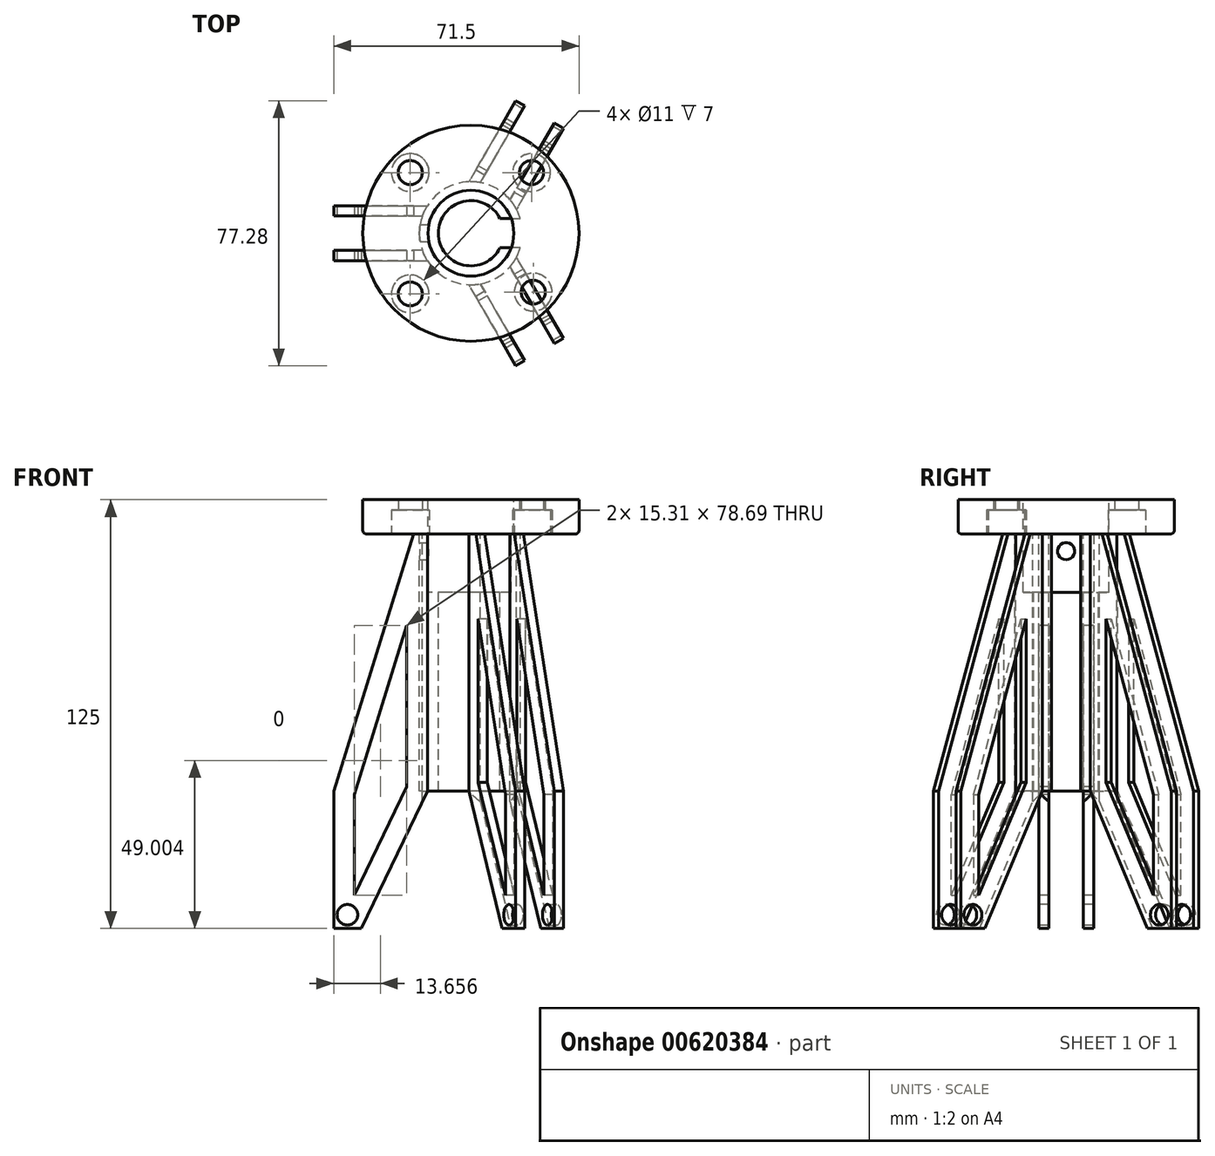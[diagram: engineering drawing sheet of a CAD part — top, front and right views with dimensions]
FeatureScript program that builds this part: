
annotation { "Feature Type Name" : "Feature", "Feature Type Description" : "" }
export const myFeature = defineFeature(function(context is Context, id is Id, definition is map)
    precondition{}
    {
        {
            var Q0;
            Q0=qCreatedBy(makeId("Top.planeOp"),FACE);
            var sketch = newSketch(context, id + "F0", { "sketchPlane" : qUnion([Q0])});
            skCircle(sketch, "E0", {"center": v(0, 0) * mm, "radius": 31.5 * mm});
            skCircle(sketch, "E1", {"center": v(0, 0) * mm, "radius": 25 * mm});
            skLineSegment(sketch, "E2", {"start": v(0, 0) * mm, "end": v(0, 25) * mm});
            skLineSegment(sketch, "E3", {"start": v(0, 0) * mm, "end": v(-17.68, 17.68) * mm});
            skCircle(sketch, "E4", {"center": v(-17.68, 17.68) * mm, "radius": 3.5 * mm});
            skLineSegment(sketch, "E5", {"start": v(0, 0) * mm, "end": v(17.68, 17.68) * mm});
            skLineSegment(sketch, "E6", {"start": v(0, 0) * mm, "end": v(0, -25) * mm});
            skLineSegment(sketch, "E7", {"start": v(0, 0) * mm, "end": v(-17.68, -17.68) * mm});
            skLineSegment(sketch, "E8", {"start": v(0.5, 0.5) * mm, "end": v(18.17, -17.17) * mm});
            skCircle(sketch, "E9", {"center": v(-17.68, -17.68) * mm, "radius": 3.5 * mm});
            skCircle(sketch, "E10", {"center": v(18.17, -17.17) * mm, "radius": 3.5 * mm});
            skCircle(sketch, "E11", {"center": v(17.68, 17.68) * mm, "radius": 3.5 * mm});
            skCircle(sketch, "E12", {"center": v(-17.68, -17.68) * mm, "radius": 5.5 * mm});
            skCircle(sketch, "E13", {"center": v(18.17, -17.17) * mm, "radius": 5.5 * mm});
            skCircle(sketch, "E14", {"center": v(17.68, 17.68) * mm, "radius": 5.5 * mm});
            skCircle(sketch, "E15", {"center": v(-17.68, 17.68) * mm, "radius": 5.5 * mm});
            skSolve(sketch);
        }
        {
            var Q0;
            Q0 = qSketchRegion(id + "F0", true);
            var Q1;
            {var subQ5=sQuery(id+"F0.wireOp",EDGE,"E4");var subQ6=sQuery(id+"F0.wireOp",EDGE,"E1");var subQ7=makeQuery(id+"F0.imprint","INTERSECT",VERTEX,{"disambiguationData":[OD(1.0)],"derivedFrom":[subQ6,subQ5]});Q1=makeQuery(id+"F0.imprint","IMPRINT",FACE,{"disambiguationData":[TD([[makeQuery(id+"F0.imprint","IMPRINT",EDGE,{"disambiguationData":[TD([[subQ7,-1.0]])],"derivedFrom":subQ6}),1.0]])]});}
            var Q2;
            {var subQ0=sQuery(id+"F0.wireOp",EDGE,"E2");Q2=makeQuery(id+"F0.imprint","IMPRINT",FACE,{"disambiguationData":[TD([[makeQuery(id+"F0.imprint","IMPRINT",EDGE,{"derivedFrom":subQ0}),1.0]])]});}
            var Q3;
            {var subQ4=sQuery(id+"F0.wireOp",EDGE,"E2");Q3=makeQuery(id+"F0.imprint","IMPRINT",FACE,{"disambiguationData":[TD([[makeQuery(id+"F0.imprint","IMPRINT",EDGE,{"derivedFrom":subQ4}),-1.0]])]});}
            var Q4;
            {var subQ5=sQuery(id+"F0.wireOp",EDGE,"E6");Q4=makeQuery(id+"F0.imprint","IMPRINT",FACE,{"disambiguationData":[TD([[makeQuery(id+"F0.imprint","IMPRINT",EDGE,{"derivedFrom":subQ5}),1.0]])]});}
            var Q5;
            {var subQ1=sQuery(id+"F0.wireOp",EDGE,"E1");var subQ7=sQuery(id+"F0.wireOp",EDGE,"E11");var subQ9=makeQuery(id+"F0.imprint","INTERSECT",VERTEX,{"disambiguationData":[OD(0.0)],"derivedFrom":[subQ1,subQ7]});Q5=makeQuery(id+"F0.imprint","IMPRINT",FACE,{"disambiguationData":[TD([[makeQuery(id+"F0.imprint","IMPRINT",EDGE,{"disambiguationData":[TD([[subQ9,1.0]])],"derivedFrom":subQ1}),1.0]])]});}
            var Q6;
            {var subQ0=sQuery(id+"F0.wireOp",EDGE,"E6");Q6=makeQuery(id+"F0.imprint","IMPRINT",FACE,{"disambiguationData":[TD([[makeQuery(id+"F0.imprint","IMPRINT",EDGE,{"derivedFrom":subQ0}),-1.0]])]});}
            var Q7;
            {var subQ1=sQuery(id+"F0.wireOp",EDGE,"E1");var subQ7=sQuery(id+"F0.wireOp",EDGE,"E14");var subQ9=makeQuery(id+"F0.imprint","INTERSECT",VERTEX,{"disambiguationData":[OD(0.0)],"derivedFrom":[subQ1,subQ7]});Q7=makeQuery(id+"F0.imprint","IMPRINT",FACE,{"disambiguationData":[TD([[makeQuery(id+"F0.imprint","IMPRINT",EDGE,{"disambiguationData":[TD([[subQ9,1.0]])],"derivedFrom":subQ1}),1.0]])]});}
            var Q8;
            {var subQ1=sQuery(id+"F0.wireOp",EDGE,"E1");var subQ7=sQuery(id+"F0.wireOp",EDGE,"E15");var subQ9=makeQuery(id+"F0.imprint","INTERSECT",VERTEX,{"disambiguationData":[OD(1.0)],"derivedFrom":[subQ1,subQ7]});Q8=makeQuery(id+"F0.imprint","IMPRINT",FACE,{"disambiguationData":[TD([[makeQuery(id+"F0.imprint","IMPRINT",EDGE,{"disambiguationData":[TD([[subQ9,-1.0]])],"derivedFrom":subQ1}),1.0]])]});}
            var Q9;
            {var subQ0=sQuery(id+"F0.wireOp",EDGE,"E10");var subQ1=sQuery(id+"F0.wireOp",EDGE,"E1");var subQ2=makeQuery(id+"F0.imprint","INTERSECT",VERTEX,{"disambiguationData":[OD(1.0)],"derivedFrom":[subQ1,subQ0]});Q9=makeQuery(id+"F0.imprint","IMPRINT",FACE,{"disambiguationData":[TD([[makeQuery(id+"F0.imprint","IMPRINT",EDGE,{"disambiguationData":[TD([[subQ2,-1.0]])],"derivedFrom":subQ1}),1.0]])]});}
            var Q10;
            {var subQ0=sQuery(id+"F0.wireOp",EDGE,"E13");var subQ1=sQuery(id+"F0.wireOp",EDGE,"E1");var subQ2=makeQuery(id+"F0.imprint","INTERSECT",VERTEX,{"disambiguationData":[OD(0.0)],"derivedFrom":[subQ1,subQ0]});Q10=makeQuery(id+"F0.imprint","IMPRINT",FACE,{"disambiguationData":[TD([[makeQuery(id+"F0.imprint","IMPRINT",EDGE,{"disambiguationData":[TD([[subQ2,-1.0]])],"derivedFrom":subQ1}),-1.0]])]});}
            var Q11;
            {var subQ0=sQuery(id+"F0.wireOp",EDGE,"E13");var subQ1=sQuery(id+"F0.wireOp",EDGE,"E1");var subQ2=makeQuery(id+"F0.imprint","INTERSECT",VERTEX,{"disambiguationData":[OD(0.0)],"derivedFrom":[subQ1,subQ0]});Q11=makeQuery(id+"F0.imprint","IMPRINT",FACE,{"disambiguationData":[TD([[makeQuery(id+"F0.imprint","IMPRINT",EDGE,{"disambiguationData":[TD([[subQ2,-1.0]])],"derivedFrom":subQ1}),1.0]])]});}
            var Q12;
            {var subQ0=sQuery(id+"F0.wireOp",EDGE,"E11");var subQ1=sQuery(id+"F0.wireOp",EDGE,"E1");var subQ2=makeQuery(id+"F0.imprint","INTERSECT",VERTEX,{"disambiguationData":[OD(1.0)],"derivedFrom":[subQ1,subQ0]});Q12=makeQuery(id+"F0.imprint","IMPRINT",FACE,{"disambiguationData":[TD([[makeQuery(id+"F0.imprint","IMPRINT",EDGE,{"disambiguationData":[TD([[subQ2,-1.0]])],"derivedFrom":subQ1}),1.0]])]});}
            var Q13;
            {var subQ0=sQuery(id+"F0.wireOp",EDGE,"E11");var subQ1=sQuery(id+"F0.wireOp",EDGE,"E1");var subQ2=makeQuery(id+"F0.imprint","INTERSECT",VERTEX,{"disambiguationData":[OD(0.0)],"derivedFrom":[subQ1,subQ0]});Q13=makeQuery(id+"F0.imprint","IMPRINT",FACE,{"disambiguationData":[TD([[makeQuery(id+"F0.imprint","IMPRINT",EDGE,{"disambiguationData":[TD([[subQ2,1.0]])],"derivedFrom":subQ1}),-1.0]])]});}
            var Q14;
            {var subQ0=sQuery(id+"F0.wireOp",EDGE,"E15");var subQ1=sQuery(id+"F0.wireOp",EDGE,"E1");var subQ2=makeQuery(id+"F0.imprint","INTERSECT",VERTEX,{"disambiguationData":[OD(0.0)],"derivedFrom":[subQ1,subQ0]});Q14=makeQuery(id+"F0.imprint","IMPRINT",FACE,{"disambiguationData":[TD([[makeQuery(id+"F0.imprint","IMPRINT",EDGE,{"disambiguationData":[TD([[subQ2,-1.0]])],"derivedFrom":subQ1}),-1.0]])]});}
            var Q15;
            {var subQ0=sQuery(id+"F0.wireOp",EDGE,"E15");var subQ1=sQuery(id+"F0.wireOp",EDGE,"E1");var subQ2=makeQuery(id+"F0.imprint","INTERSECT",VERTEX,{"disambiguationData":[OD(0.0)],"derivedFrom":[subQ1,subQ0]});Q15=makeQuery(id+"F0.imprint","IMPRINT",FACE,{"disambiguationData":[TD([[makeQuery(id+"F0.imprint","IMPRINT",EDGE,{"disambiguationData":[TD([[subQ2,-1.0]])],"derivedFrom":subQ1}),1.0]])]});}
            var Q16;
            {var subQ0=sQuery(id+"F0.wireOp",EDGE,"E12");var subQ1=sQuery(id+"F0.wireOp",EDGE,"E1");var subQ2=makeQuery(id+"F0.imprint","INTERSECT",VERTEX,{"disambiguationData":[OD(0.0)],"derivedFrom":[subQ1,subQ0]});Q16=makeQuery(id+"F0.imprint","IMPRINT",FACE,{"disambiguationData":[TD([[makeQuery(id+"F0.imprint","IMPRINT",EDGE,{"disambiguationData":[TD([[subQ2,-1.0]])],"derivedFrom":subQ1}),-1.0]])]});}
            var Q17;
            {var subQ0=sQuery(id+"F0.wireOp",EDGE,"E12");var subQ1=sQuery(id+"F0.wireOp",EDGE,"E1");var subQ2=makeQuery(id+"F0.imprint","INTERSECT",VERTEX,{"disambiguationData":[OD(0.0)],"derivedFrom":[subQ1,subQ0]});Q17=makeQuery(id+"F0.imprint","IMPRINT",FACE,{"disambiguationData":[TD([[makeQuery(id+"F0.imprint","IMPRINT",EDGE,{"disambiguationData":[TD([[subQ2,-1.0]])],"derivedFrom":subQ1}),1.0]])]});}
            var Q18;
            {var subQ0=sQuery(id+"F0.wireOp",EDGE,"E9");var subQ1=sQuery(id+"F0.wireOp",EDGE,"E1");var subQ2=makeQuery(id+"F0.imprint","INTERSECT",VERTEX,{"disambiguationData":[OD(1.0)],"derivedFrom":[subQ1,subQ0]});Q18=makeQuery(id+"F0.imprint","IMPRINT",FACE,{"disambiguationData":[TD([[makeQuery(id+"F0.imprint","IMPRINT",EDGE,{"disambiguationData":[TD([[subQ2,-1.0]])],"derivedFrom":subQ1}),1.0]])]});}
            extrude(context, id + "F1", {"entities" : qUnion([Q0, Q1, Q2, Q3, Q4, Q5, Q6, Q7, Q8, Q9, Q10, Q11, Q12, Q13, Q14, Q15, Q16, Q17, Q18]), "depth" : 10 * mm, "offsetDistance" : 25 * mm});
        }
        {
            var Q0;
            {var subQ0=sQuery(id+"F0.wireOp",EDGE,"E12");var subQ1=sQuery(id+"F0.wireOp",EDGE,"E1");var subQ2=makeQuery(id+"F0.imprint","INTERSECT",VERTEX,{"disambiguationData":[OD(0.0)],"derivedFrom":[subQ1,subQ0]});Q0=makeQuery(id+"F0.imprint","IMPRINT",FACE,{"disambiguationData":[TD([[makeQuery(id+"F0.imprint","IMPRINT",EDGE,{"disambiguationData":[TD([[subQ2,-1.0]])],"derivedFrom":subQ1}),-1.0]])]});}
            var Q1;
            {var subQ0=sQuery(id+"F0.wireOp",EDGE,"E12");var subQ1=sQuery(id+"F0.wireOp",EDGE,"E1");var subQ2=makeQuery(id+"F0.imprint","INTERSECT",VERTEX,{"disambiguationData":[OD(0.0)],"derivedFrom":[subQ1,subQ0]});Q1=makeQuery(id+"F0.imprint","IMPRINT",FACE,{"disambiguationData":[TD([[makeQuery(id+"F0.imprint","IMPRINT",EDGE,{"disambiguationData":[TD([[subQ2,-1.0]])],"derivedFrom":subQ1}),1.0]])]});}
            var Q2;
            {var subQ0=sQuery(id+"F0.wireOp",EDGE,"E9");var subQ1=sQuery(id+"F0.wireOp",EDGE,"E1");var subQ2=makeQuery(id+"F0.imprint","INTERSECT",VERTEX,{"disambiguationData":[OD(1.0)],"derivedFrom":[subQ1,subQ0]});Q2=makeQuery(id+"F0.imprint","IMPRINT",FACE,{"disambiguationData":[TD([[makeQuery(id+"F0.imprint","IMPRINT",EDGE,{"disambiguationData":[TD([[subQ2,-1.0]])],"derivedFrom":subQ1}),1.0]])]});}
            var Q3;
            {var subQ0=sQuery(id+"F0.wireOp",EDGE,"E13");var subQ1=sQuery(id+"F0.wireOp",EDGE,"E1");var subQ2=makeQuery(id+"F0.imprint","INTERSECT",VERTEX,{"disambiguationData":[OD(0.0)],"derivedFrom":[subQ1,subQ0]});Q3=makeQuery(id+"F0.imprint","IMPRINT",FACE,{"disambiguationData":[TD([[makeQuery(id+"F0.imprint","IMPRINT",EDGE,{"disambiguationData":[TD([[subQ2,-1.0]])],"derivedFrom":subQ1}),1.0]])]});}
            var Q4;
            {var subQ0=sQuery(id+"F0.wireOp",EDGE,"E10");var subQ1=sQuery(id+"F0.wireOp",EDGE,"E1");var subQ2=makeQuery(id+"F0.imprint","INTERSECT",VERTEX,{"disambiguationData":[OD(1.0)],"derivedFrom":[subQ1,subQ0]});Q4=makeQuery(id+"F0.imprint","IMPRINT",FACE,{"disambiguationData":[TD([[makeQuery(id+"F0.imprint","IMPRINT",EDGE,{"disambiguationData":[TD([[subQ2,-1.0]])],"derivedFrom":subQ1}),1.0]])]});}
            var Q5;
            {var subQ0=sQuery(id+"F0.wireOp",EDGE,"E13");var subQ1=sQuery(id+"F0.wireOp",EDGE,"E1");var subQ2=makeQuery(id+"F0.imprint","INTERSECT",VERTEX,{"disambiguationData":[OD(0.0)],"derivedFrom":[subQ1,subQ0]});Q5=makeQuery(id+"F0.imprint","IMPRINT",FACE,{"disambiguationData":[TD([[makeQuery(id+"F0.imprint","IMPRINT",EDGE,{"disambiguationData":[TD([[subQ2,-1.0]])],"derivedFrom":subQ1}),-1.0]])]});}
            var Q6;
            {var subQ0=sQuery(id+"F0.wireOp",EDGE,"E15");var subQ1=sQuery(id+"F0.wireOp",EDGE,"E1");var subQ2=makeQuery(id+"F0.imprint","INTERSECT",VERTEX,{"disambiguationData":[OD(0.0)],"derivedFrom":[subQ1,subQ0]});Q6=makeQuery(id+"F0.imprint","IMPRINT",FACE,{"disambiguationData":[TD([[makeQuery(id+"F0.imprint","IMPRINT",EDGE,{"disambiguationData":[TD([[subQ2,-1.0]])],"derivedFrom":subQ1}),-1.0]])]});}
            var Q7;
            {var subQ0=sQuery(id+"F0.wireOp",EDGE,"E4");var subQ1=sQuery(id+"F0.wireOp",EDGE,"E1");var subQ2=makeQuery(id+"F0.imprint","INTERSECT",VERTEX,{"disambiguationData":[OD(1.0)],"derivedFrom":[subQ1,subQ0]});Q7=makeQuery(id+"F0.imprint","IMPRINT",FACE,{"disambiguationData":[TD([[makeQuery(id+"F0.imprint","IMPRINT",EDGE,{"disambiguationData":[TD([[subQ2,-1.0]])],"derivedFrom":subQ1}),1.0]])]});}
            var Q8;
            {var subQ0=sQuery(id+"F0.wireOp",EDGE,"E15");var subQ1=sQuery(id+"F0.wireOp",EDGE,"E1");var subQ2=makeQuery(id+"F0.imprint","INTERSECT",VERTEX,{"disambiguationData":[OD(0.0)],"derivedFrom":[subQ1,subQ0]});Q8=makeQuery(id+"F0.imprint","IMPRINT",FACE,{"disambiguationData":[TD([[makeQuery(id+"F0.imprint","IMPRINT",EDGE,{"disambiguationData":[TD([[subQ2,-1.0]])],"derivedFrom":subQ1}),1.0]])]});}
            var Q9;
            {var subQ0=sQuery(id+"F0.wireOp",EDGE,"E11");var subQ1=sQuery(id+"F0.wireOp",EDGE,"E1");var subQ2=makeQuery(id+"F0.imprint","INTERSECT",VERTEX,{"disambiguationData":[OD(1.0)],"derivedFrom":[subQ1,subQ0]});Q9=makeQuery(id+"F0.imprint","IMPRINT",FACE,{"disambiguationData":[TD([[makeQuery(id+"F0.imprint","IMPRINT",EDGE,{"disambiguationData":[TD([[subQ2,-1.0]])],"derivedFrom":subQ1}),1.0]])]});}
            var Q10;
            {var subQ0=sQuery(id+"F0.wireOp",EDGE,"E11");var subQ1=sQuery(id+"F0.wireOp",EDGE,"E1");var subQ2=makeQuery(id+"F0.imprint","INTERSECT",VERTEX,{"disambiguationData":[OD(0.0)],"derivedFrom":[subQ1,subQ0]});Q10=makeQuery(id+"F0.imprint","IMPRINT",FACE,{"disambiguationData":[TD([[makeQuery(id+"F0.imprint","IMPRINT",EDGE,{"disambiguationData":[TD([[subQ2,1.0]])],"derivedFrom":subQ1}),-1.0]])]});}
            var Q11;
            {var subQ0=sQuery(id+"F0.wireOp",EDGE,"E11");var subQ1=sQuery(id+"F0.wireOp",EDGE,"E1");var subQ2=makeQuery(id+"F0.imprint","INTERSECT",VERTEX,{"disambiguationData":[OD(0.0)],"derivedFrom":[subQ1,subQ0]});Q11=makeQuery(id+"F0.imprint","IMPRINT",FACE,{"disambiguationData":[TD([[makeQuery(id+"F0.imprint","IMPRINT",EDGE,{"disambiguationData":[TD([[subQ2,1.0]])],"derivedFrom":subQ1}),1.0]])]});}
            extrude(context, id + "F2", {"entities" : qUnion([Q0, Q1, Q2, Q3, Q4, Q5, Q6, Q7, Q8, Q9, Q10, Q11]), "operationType" : NewBodyOperationType.REMOVE, "depth" : 7 * mm, "offsetDistance" : 25 * mm});
        }
        {
            var Q0;
            Q0=makeQuery(id+"F1.opExtrude","CAP_FACE",FACE,{"disambiguationData":[OSD([sQuery(id+"F0.wireOp",EDGE,"E0"),sQuery(id+"F0.wireOp",EDGE,"E4"),sQuery(id+"F0.wireOp",EDGE,"E9"),sQuery(id+"F0.wireOp",EDGE,"E10"),sQuery(id+"F0.wireOp",EDGE,"E11")])],"isStart":true});
            var sketch = newSketch(context, id + "F3", { "sketchPlane" : qUnion([Q0])});
            skArc(sketch, "E16", {"start": v(8.5, 4.25) * mm, "mid": v(-9.5, 0) * mm, "end": v(8.5, -4.25) * mm});
            skArc(sketch, "E17", {"start": v(14.39, 4.25) * mm, "mid": v(-15, 0) * mm, "end": v(14.39, -4.25) * mm});
            skLineSegment(sketch, "E18", {"start": v(14.39, 4.25) * mm, "end": v(8.5, 4.25) * mm});
            skLineSegment(sketch, "E19", {"start": v(8.5, -4.25) * mm, "end": v(14.39, -4.25) * mm});
            skPoint(sketch, "E20.start.orphan", {"position": v(15, -4.25) * mm});
            skPoint(sketch, "E21.orphan", {"position": v(1.1, 0) * mm});
            skPoint(sketch, "E22.end.orphan", {"position": v(15, 0) * mm});
            skLineSegment(sketch, "E23", {"start": v(0, 0) * mm, "end": v(7.5, 13) * mm});
            skLineSegment(sketch, "E24", {"start": v(0, 0) * mm, "end": v(-15, 0) * mm});
            skLineSegment(sketch, "E25", {"start": v(0, 0) * mm, "end": v(7.5, -13) * mm});
            skLineSegment(sketch, "E26", {"start": v(18.5, -17.03) * mm, "end": v(20.23, -16.03) * mm});
            skLineSegment(sketch, "E27", {"start": v(3.17, 15.5) * mm, "end": v(15.67, 37.14) * mm});
            skLineSegment(sketch, "E28", {"start": v(15.67, 37.14) * mm, "end": v(13.07, 38.64) * mm});
            skLineSegment(sketch, "E29", {"start": v(13.07, 38.64) * mm, "end": v(-0.58, 14.99) * mm});
            skLineSegment(sketch, "E30", {"start": v(3.17, 15.5) * mm, "end": v(2.74, 14.75) * mm});
            skLineSegment(sketch, "E31", {"start": v(11.83, 10.5) * mm, "end": v(24.33, 32.14) * mm});
            skLineSegment(sketch, "E32", {"start": v(24.33, 32.14) * mm, "end": v(26.93, 30.64) * mm});
            skLineSegment(sketch, "E33", {"start": v(26.93, 30.64) * mm, "end": v(13.27, 6.99) * mm});
            skLineSegment(sketch, "E34", {"start": v(11.83, 10.5) * mm, "end": v(11.4, 9.75) * mm});
            skLineSegment(sketch, "E35", {"start": v(-15, 0) * mm, "end": v(-15, 5) * mm});
            skLineSegment(sketch, "E36", {"start": v(-15, 5) * mm, "end": v(-40, 5) * mm});
            skLineSegment(sketch, "E37", {"start": v(-15, 5) * mm, "end": v(-14.14, 5) * mm});
            skLineSegment(sketch, "E38", {"start": v(-15, 0) * mm, "end": v(-15, -5) * mm});
            skLineSegment(sketch, "E39", {"start": v(-40, 5) * mm, "end": v(-40, 8) * mm});
            skLineSegment(sketch, "E40", {"start": v(-40, 8) * mm, "end": v(-12.69, 8) * mm});
            skLineSegment(sketch, "E41", {"start": v(3.17, -15.5) * mm, "end": v(15.67, -37.14) * mm});
            skLineSegment(sketch, "E42", {"start": v(15.67, -37.14) * mm, "end": v(13.07, -38.64) * mm});
            skLineSegment(sketch, "E43", {"start": v(13.07, -38.64) * mm, "end": v(-0.58, -14.99) * mm});
            skLineSegment(sketch, "E44", {"start": v(11.83, -10.5) * mm, "end": v(24.33, -32.14) * mm});
            skLineSegment(sketch, "E45", {"start": v(24.33, -32.14) * mm, "end": v(26.93, -30.64) * mm});
            skLineSegment(sketch, "E46", {"start": v(26.93, -30.64) * mm, "end": v(13.27, -6.99) * mm});
            skLineSegment(sketch, "E47", {"start": v(11.83, -10.5) * mm, "end": v(11.4, -9.75) * mm});
            skLineSegment(sketch, "E48", {"start": v(3.17, -15.5) * mm, "end": v(2.74, -14.75) * mm});
            skLineSegment(sketch, "E49", {"start": v(-15, -5) * mm, "end": v(-40, -5) * mm});
            skLineSegment(sketch, "E50", {"start": v(-40, -5) * mm, "end": v(-40, -8) * mm});
            skLineSegment(sketch, "E51", {"start": v(-40, -8) * mm, "end": v(-12.69, -8) * mm});
            skLineSegment(sketch, "E52", {"start": v(-15, -5) * mm, "end": v(-14.14, -5) * mm});
            skSolve(sketch);
        }
        {
            var Q0;
            Q0=makeQuery(id+"F3.imprint","IMPRINT",FACE,{"disambiguationData":[TD([[makeQuery(id+"F3.imprint","IMPRINT",EDGE,{"derivedFrom":sQuery(id+"F3.wireOp",EDGE,"27czpzdm-gOxT-79nV-ukG3-qy1ORN0447aD")}),1.0]])]});
            var Q1;
            Q1=makeQuery(id+"F3.imprint","IMPRINT",FACE,{"disambiguationData":[TD([[makeQuery(id+"F3.imprint","IMPRINT",EDGE,{"derivedFrom":sQuery(id+"F3.wireOp",EDGE,"uuFctwZB-QEf3-xh13-IUdi-1K9DjAXxjuxu")}),-1.0]])]});
            var Q2;
            Q2=makeQuery(id+"F3.imprint","IMPRINT",FACE,{"disambiguationData":[TD([[makeQuery(id+"F3.imprint","IMPRINT",EDGE,{"derivedFrom":sQuery(id+"F3.wireOp",EDGE,"3tihZK4Q-J3YK-7ihB-wwWK-0AjhGr4ynaBD")}),1.0]])]});
            var Q3;
            Q3=makeQuery(id+"F3.imprint","IMPRINT",FACE,{"disambiguationData":[TD([[makeQuery(id+"F3.imprint","IMPRINT",EDGE,{"derivedFrom":sQuery(id+"F3.wireOp",EDGE,"P91pi9WV-s5ji-Orfy-RXOP-pitRkdTstdLn")}),-1.0]])]});
            var Q4;
            {var subQ4=sQuery(id+"F3.wireOp",EDGE,"E18");Q4=makeQuery(id+"F3.imprint","IMPRINT",FACE,{"disambiguationData":[TD([[makeQuery(id+"F3.imprint","IMPRINT",EDGE,{"derivedFrom":subQ4}),-1.0]])]});}
            var Q5;
            {var subQ0=sQuery(id+"F3.wireOp",EDGE,"E19");Q5=makeQuery(id+"F3.imprint","IMPRINT",FACE,{"disambiguationData":[TD([[makeQuery(id+"F3.imprint","IMPRINT",EDGE,{"derivedFrom":subQ0}),-1.0]])]});}
            var Q6;
            {var subQ4=sQuery(id+"F3.wireOp",EDGE,"E23");var subQ6=sQuery(id+"F3.wireOp",EDGE,"E16");var subQ7=makeQuery(id+"F3.imprint","INTERSECT",VERTEX,{"derivedFrom":[subQ6,subQ4]});Q6=makeQuery(id+"F3.imprint","IMPRINT",FACE,{"disambiguationData":[TD([[makeQuery(id+"F3.imprint","IMPRINT",EDGE,{"disambiguationData":[TD([[subQ7,-1.0]])],"derivedFrom":subQ6}),-1.0]])]});}
            var Q7;
            {var subQ3=sQuery(id+"F3.wireOp",EDGE,"E24");var subQ5=sQuery(id+"F3.wireOp",EDGE,"E16");var subQ6=makeQuery(id+"F3.imprint","INTERSECT",VERTEX,{"derivedFrom":[subQ5,subQ3]});Q7=makeQuery(id+"F3.imprint","IMPRINT",FACE,{"disambiguationData":[TD([[makeQuery(id+"F3.imprint","IMPRINT",EDGE,{"disambiguationData":[TD([[subQ6,-1.0]])],"derivedFrom":subQ5}),-1.0]])]});}
            var Q8;
            {var subQ0=sQuery(id+"F3.wireOp",EDGE,"jUfSCTw1-h4xW-kg2C-D6uF-oDkjy2WKzLZC");Q8=makeQuery(id+"F3.imprint","IMPRINT",FACE,{"disambiguationData":[TD([[makeQuery(id+"F3.imprint","IMPRINT",EDGE,{"derivedFrom":subQ0}),1.0]])]});}
            var Q9;
            {var subQ0=sQuery(id+"F3.wireOp",EDGE,"PDN8pKsh-MS3S-zusk-sD9p-XKP6C9vrnxKT");Q9=makeQuery(id+"F3.imprint","IMPRINT",FACE,{"disambiguationData":[TD([[makeQuery(id+"F3.imprint","IMPRINT",EDGE,{"derivedFrom":subQ0}),-1.0]])]});}
            var Q10;
            {var subQ0=sQuery(id+"F3.wireOp",EDGE,"E26");Q10=makeQuery(id+"F3.imprint","IMPRINT",FACE,{"disambiguationData":[TD([[makeQuery(id+"F3.imprint","IMPRINT",EDGE,{"derivedFrom":subQ0}),1.0]])]});}
            var Q11;
            {var subQ0=sQuery(id+"F3.wireOp",EDGE,"h3JoUdTA-LX2n-yNLR-IDpX-qLHGJsSSBT1F");Q11=makeQuery(id+"F3.imprint","IMPRINT",FACE,{"disambiguationData":[TD([[makeQuery(id+"F3.imprint","IMPRINT",EDGE,{"derivedFrom":subQ0}),-1.0]])]});}
            var Q12;
            {var subQ5=sQuery(id+"F3.wireOp",EDGE,"E37");Q12=makeQuery(id+"F3.imprint","IMPRINT",FACE,{"disambiguationData":[TD([[makeQuery(id+"F3.imprint","IMPRINT",EDGE,{"derivedFrom":subQ5}),1.0]])]});}
            var Q13;
            {var subQ0=sQuery(id+"F3.wireOp",EDGE,"E52");Q13=makeQuery(id+"F3.imprint","IMPRINT",FACE,{"disambiguationData":[TD([[makeQuery(id+"F3.imprint","IMPRINT",EDGE,{"derivedFrom":subQ0}),-1.0]])]});}
            var Q14;
            {var subQ0=sQuery(id+"F3.wireOp",EDGE,"E39");Q14=makeQuery(id+"F3.imprint","IMPRINT",FACE,{"disambiguationData":[TD([[makeQuery(id+"F3.imprint","IMPRINT",EDGE,{"derivedFrom":subQ0}),-1.0]])]});}
            var Q15;
            {var subQ0=sQuery(id+"F3.wireOp",EDGE,"E50");Q15=makeQuery(id+"F3.imprint","IMPRINT",FACE,{"disambiguationData":[TD([[makeQuery(id+"F3.imprint","IMPRINT",EDGE,{"derivedFrom":subQ0}),1.0]])]});}
            var Q16;
            {var subQ0=sQuery(id+"F3.wireOp",EDGE,"E48");Q16=makeQuery(id+"F3.imprint","IMPRINT",FACE,{"disambiguationData":[TD([[makeQuery(id+"F3.imprint","IMPRINT",EDGE,{"derivedFrom":subQ0}),1.0]])]});}
            var Q17;
            {var subQ5=sQuery(id+"F3.wireOp",EDGE,"E47");Q17=makeQuery(id+"F3.imprint","IMPRINT",FACE,{"disambiguationData":[TD([[makeQuery(id+"F3.imprint","IMPRINT",EDGE,{"derivedFrom":subQ5}),-1.0]])]});}
            var Q18;
            {var subQ0=sQuery(id+"F3.wireOp",EDGE,"E46");var subQ1=makeQuery(id+"F3.imprint","IMPRINT",VERTEX,{"derivedFrom":subQ0});Q18=makeQuery(id+"F3.imprint","IMPRINT",FACE,{"disambiguationData":[TD([[makeQuery(id+"F3.imprint","IMPRINT",EDGE,{"disambiguationData":[TD([[subQ1,1.0]])],"derivedFrom":subQ0}),1.0]])]});}
            var Q19;
            {var subQ0=sQuery(id+"F3.wireOp",EDGE,"E44");var subQ1=makeQuery(id+"F1.opExtrude","CAP_EDGE",EDGE,{"disambiguationData":[OSD([sQuery(id+"F0.wireOp",EDGE,"E0")])],"isStart":true});var subQ2=makeQuery(id+"F3.imprint","INTERSECT",VERTEX,{"derivedFrom":[subQ1,subQ0]});Q19=makeQuery(id+"F3.imprint","IMPRINT",FACE,{"disambiguationData":[TD([[makeQuery(id+"F3.imprint","IMPRINT",EDGE,{"disambiguationData":[TD([[subQ2,1.0]])],"derivedFrom":subQ0}),1.0]])]});}
            var Q20;
            {var subQ5=sQuery(id+"F3.wireOp",EDGE,"E30");Q20=makeQuery(id+"F3.imprint","IMPRINT",FACE,{"disambiguationData":[TD([[makeQuery(id+"F3.imprint","IMPRINT",EDGE,{"derivedFrom":subQ5}),-1.0]])]});}
            var Q21;
            {var subQ0=sQuery(id+"F3.wireOp",EDGE,"E42");Q21=makeQuery(id+"F3.imprint","IMPRINT",FACE,{"disambiguationData":[TD([[makeQuery(id+"F3.imprint","IMPRINT",EDGE,{"derivedFrom":subQ0}),-1.0]])]});}
            var Q22;
            {var subQ0=sQuery(id+"F3.wireOp",EDGE,"E45");Q22=makeQuery(id+"F3.imprint","IMPRINT",FACE,{"disambiguationData":[TD([[makeQuery(id+"F3.imprint","IMPRINT",EDGE,{"derivedFrom":subQ0}),1.0]])]});}
            var Q23;
            {var subQ0=sQuery(id+"F3.wireOp",EDGE,"E31");var subQ1=makeQuery(id+"F1.opExtrude","CAP_EDGE",EDGE,{"disambiguationData":[OSD([sQuery(id+"F0.wireOp",EDGE,"E0")])],"isStart":true});var subQ2=makeQuery(id+"F3.imprint","INTERSECT",VERTEX,{"derivedFrom":[subQ1,subQ0]});Q23=makeQuery(id+"F3.imprint","IMPRINT",FACE,{"disambiguationData":[TD([[makeQuery(id+"F3.imprint","IMPRINT",EDGE,{"disambiguationData":[TD([[subQ2,1.0]])],"derivedFrom":subQ0}),-1.0]])]});}
            var Q24;
            {var subQ0=sQuery(id+"F3.wireOp",EDGE,"E32");Q24=makeQuery(id+"F3.imprint","IMPRINT",FACE,{"disambiguationData":[TD([[makeQuery(id+"F3.imprint","IMPRINT",EDGE,{"derivedFrom":subQ0}),-1.0]])]});}
            var Q25;
            {var subQ0=sQuery(id+"F3.wireOp",EDGE,"E28");Q25=makeQuery(id+"F3.imprint","IMPRINT",FACE,{"disambiguationData":[TD([[makeQuery(id+"F3.imprint","IMPRINT",EDGE,{"derivedFrom":subQ0}),1.0]])]});}
            var Q26;
            {var subQ0=sQuery(id+"F3.wireOp",EDGE,"E34");Q26=makeQuery(id+"F3.imprint","IMPRINT",FACE,{"disambiguationData":[TD([[makeQuery(id+"F3.imprint","IMPRINT",EDGE,{"derivedFrom":subQ0}),1.0]])]});}
            var Q27;
            {var subQ0=sQuery(id+"F3.wireOp",EDGE,"E31");var subQ1=makeQuery(id+"F2.boolean.opBoolean","COPY",EDGE,{"derivedFrom":makeQuery(id+"F2.opExtrude","CAP_EDGE",EDGE,{"disambiguationData":[OSD([sQuery(id+"F0.wireOp",EDGE,"E13")])],"isStart":true})});var subQ2=makeQuery(id+"F3.imprint","INTERSECT",VERTEX,{"disambiguationData":[OD(0.0)],"derivedFrom":[subQ1,subQ0]});Q27=makeQuery(id+"F3.imprint","IMPRINT",FACE,{"disambiguationData":[TD([[makeQuery(id+"F3.imprint","IMPRINT",EDGE,{"disambiguationData":[TD([[subQ2,-1.0]])],"derivedFrom":subQ0}),-1.0]])]});}
            extrude(context, id + "F4", {"entities" : qUnion([Q0, Q1, Q2, Q3, Q4, Q5, Q6, Q7, Q8, Q9, Q10, Q11, Q12, Q13, Q14, Q15, Q16, Q17, Q18, Q19, Q20, Q21, Q22, Q23, Q24, Q25, Q26, Q27]), "operationType" : NewBodyOperationType.ADD, "depth" : 75 * mm, "offsetDistance" : 25 * mm});
        }
        {
            var Q0;
            Q0=makeQuery(id+"F4.opExtrude","CAP_FACE",FACE,{"disambiguationData":[OSD([sQuery(id+"F3.wireOp",EDGE,"E16"),sQuery(id+"F3.wireOp",EDGE,"E17"),sQuery(id+"F3.wireOp",EDGE,"E18"),sQuery(id+"F3.wireOp",EDGE,"E19"),sQuery(id+"F3.wireOp",EDGE,"uuFctwZB-QEf3-xh13-IUdi-1K9DjAXxjuxu"),sQuery(id+"F3.wireOp",EDGE,"lA2qv6hN-rxdL-ykno-SuZh-oJRq7noH7ACG"),sQuery(id+"F3.wireOp",EDGE,"6xB6c5hb-OY1l-nDjD-XPZR-9SyL3sMmdLtA"),sQuery(id+"F3.wireOp",EDGE,"3tihZK4Q-J3YK-7ihB-wwWK-0AjhGr4ynaBD"),sQuery(id+"F3.wireOp",EDGE,"nUsjtnsL-exj4-lQ8A-9jKv-JqzfBqHrXNOA"),sQuery(id+"F3.wireOp",EDGE,"TqBnyhGr-CcaL-aKuj-MYkN-2bOTyf4QL2CP"),sQuery(id+"F3.wireOp",EDGE,"P91pi9WV-s5ji-Orfy-RXOP-pitRkdTstdLn"),sQuery(id+"F3.wireOp",EDGE,"qgwGtvcS-NxAi-QZZZ-aVZE-ern4TRvHe4dv"),sQuery(id+"F3.wireOp",EDGE,"c18IXUts-G2ux-vmbx-LoeI-X3mpEr3HK6q8"),sQuery(id+"F3.wireOp",EDGE,"NtNiX4Or-bpP6-DFtE-pZVk-ywg64M319E2C"),sQuery(id+"F3.wireOp",EDGE,"7VfsG0oY-yPZK-3RAR-ovIo-EdMV0O4nZmDE"),sQuery(id+"F3.wireOp",EDGE,"E26"),sQuery(id+"F3.wireOp",EDGE,"PBJ80vdM-MJwH-6Xol-lynH-db3yzdXyK4RM"),sQuery(id+"F3.wireOp",EDGE,"yNWTSE8S-Jr9G-um06-3xJp-LWfp4sMIJ7eS"),sQuery(id+"F3.wireOp",EDGE,"h3JoUdTA-LX2n-yNLR-IDpX-qLHGJsSSBT1F"),sQuery(id+"F3.wireOp",EDGE,"E3YIzRBm-b0cc-3mfu-vOTC-etVTTVF42Bcp"),sQuery(id+"F3.wireOp",EDGE,"27czpzdm-gOxT-79nV-ukG3-qy1ORN0447aD"),sQuery(id+"F3.wireOp",EDGE,"eAhfjK3V-2ton-WzI9-PRfh-kVvZqgzJAoIv"),sQuery(id+"F3.wireOp",EDGE,"4z0P0KiG-cDOP-e5GR-tbla-39WZwBQgtr8r"),sQuery(id+"F3.wireOp",EDGE,"kT4ZFHPe-VBeY-gfbn-EbjU-Du8JkESP1seN"),sQuery(id+"F3.wireOp",EDGE,"jUfSCTw1-h4xW-kg2C-D6uF-oDkjy2WKzLZC"),sQuery(id+"F3.wireOp",EDGE,"6kDt0kpZ-CR8h-vkfm-t620-kVocVSu40wqg"),sQuery(id+"F3.wireOp",EDGE,"b7XTW9ox-wLUN-RSvt-gVR8-fDOOiMKAazzL"),sQuery(id+"F3.wireOp",EDGE,"PDN8pKsh-MS3S-zusk-sD9p-XKP6C9vrnxKT")])],"isStart":false});
            var sketch = newSketch(context, id + "F5", { "sketchPlane" : qUnion([Q0])});
            skCircle(sketch, "E53", {"center": v(0, 0) * mm, "radius": 15 * mm});
            skSolve(sketch);
        }
        {
            var Q0;
            Q0=makeQuery(id+"F5.imprint","IMPRINT",FACE,{"disambiguationData":[TD([[makeQuery(id+"F5.imprint","IMPRINT",EDGE,{"derivedFrom":makeQuery(id+"F4.opExtrude","CAP_EDGE",EDGE,{"disambiguationData":[OSD([sQuery(id+"F3.wireOp",EDGE,"E28")])],"isStart":false})}),1.0]])]});
            var Q1;
            Q1=makeQuery(id+"F5.imprint","IMPRINT",FACE,{"disambiguationData":[TD([[makeQuery(id+"F5.imprint","IMPRINT",EDGE,{"derivedFrom":makeQuery(id+"F4.opExtrude","CAP_EDGE",EDGE,{"disambiguationData":[OSD([sQuery(id+"F3.wireOp",EDGE,"E32")])],"isStart":false})}),-1.0]])]});
            var Q2;
            Q2=makeQuery(id+"F5.imprint","IMPRINT",FACE,{"disambiguationData":[TD([[makeQuery(id+"F5.imprint","IMPRINT",EDGE,{"derivedFrom":makeQuery(id+"F4.opExtrude","CAP_EDGE",EDGE,{"disambiguationData":[OSD([sQuery(id+"F3.wireOp",EDGE,"E45")])],"isStart":false})}),1.0]])]});
            var Q3;
            Q3=makeQuery(id+"F5.imprint","IMPRINT",FACE,{"disambiguationData":[TD([[makeQuery(id+"F5.imprint","IMPRINT",EDGE,{"derivedFrom":makeQuery(id+"F4.opExtrude","CAP_EDGE",EDGE,{"disambiguationData":[OSD([sQuery(id+"F3.wireOp",EDGE,"E42")])],"isStart":false})}),-1.0]])]});
            var Q4;
            Q4=makeQuery(id+"F5.imprint","IMPRINT",FACE,{"disambiguationData":[TD([[makeQuery(id+"F5.imprint","IMPRINT",EDGE,{"derivedFrom":makeQuery(id+"F4.opExtrude","CAP_EDGE",EDGE,{"disambiguationData":[OSD([sQuery(id+"F3.wireOp",EDGE,"E50")])],"isStart":false})}),1.0]])]});
            var Q5;
            Q5=makeQuery(id+"F5.imprint","IMPRINT",FACE,{"disambiguationData":[TD([[makeQuery(id+"F5.imprint","IMPRINT",EDGE,{"derivedFrom":makeQuery(id+"F4.opExtrude","CAP_EDGE",EDGE,{"disambiguationData":[OSD([sQuery(id+"F3.wireOp",EDGE,"E39")])],"isStart":false})}),-1.0]])]});
            extrude(context, id + "F6", {"entities" : qUnion([Q0, Q1, Q2, Q3, Q4, Q5]), "operationType" : NewBodyOperationType.ADD, "depth" : 40 * mm, "offsetDistance" : 25 * mm});
        }
        {
            var Q0;
            {var subQ0=sQuery(id+"F3.wireOp",EDGE,"E46");Q0=makeQuery(id+"F6.boolean.opBoolean","MERGE",FACE,{"derivedFrom":[makeQuery(id+"F4.opExtrude","SWEPT_FACE",FACE,{"disambiguationData":[OSD([subQ0])]}),makeQuery(id+"F6.opExtrude","SWEPT_FACE",FACE,{"disambiguationData":[OSD([subQ0])]})]});}
            var sketch = newSketch(context, id + "F7", { "sketchPlane" : qUnion([Q0])});
            skLineSegment(sketch, "E54", {"start": v(40, -115) * mm, "end": v(36, -115) * mm});
            skLineSegment(sketch, "E55", {"start": v(36, -115) * mm, "end": v(36, -111) * mm});
            skCircle(sketch, "E56", {"center": v(36, -111) * mm, "radius": 3 * mm});
            skLineSegment(sketch, "E57", {"start": v(12.69, -75) * mm, "end": v(40, -75) * mm});
            skLineSegment(sketch, "E58", {"start": v(12.69, 0) * mm, "end": v(16.69, 0) * mm});
            skLineSegment(sketch, "E59", {"start": v(16.69, 0) * mm, "end": v(40, -75) * mm});
            skLineSegment(sketch, "E60", {"start": v(40, -115) * mm, "end": v(32, -115) * mm});
            skLineSegment(sketch, "E61", {"start": v(32, -115) * mm, "end": v(12.69, -75) * mm});
            skSolve(sketch);
        }
        {
            var Q0;
            Q0 = qSketchRegion(id + "F7", true);
            var Q1;
            {var subQ13=sQuery(id+"F7.wireOp",EDGE,"E59");Q1=makeQuery(id+"F7.imprint","IMPRINT",FACE,{"disambiguationData":[TD([[makeQuery(id+"F7.imprint","IMPRINT",EDGE,{"derivedFrom":subQ13}),1.0]])]});}
            var Q2;
            {var subQ0=sQuery(id+"F7.wireOp",EDGE,"E61");Q2=makeQuery(id+"F7.imprint","IMPRINT",FACE,{"disambiguationData":[TD([[makeQuery(id+"F7.imprint","IMPRINT",EDGE,{"derivedFrom":subQ0}),1.0]])]});}
            extrude(context, id + "F8", {"entities" : qUnion([Q0, Q1, Q2]), "operationType" : NewBodyOperationType.REMOVE, "oppositeDirection" : true, "depth" : 16 * mm, "offsetDistance" : 25 * mm});
        }
        {
            var Q0;
            {var subQ0=sQuery(id+"F3.wireOp",EDGE,"E40");Q0=makeQuery(id+"F6.boolean.opBoolean","MERGE",FACE,{"derivedFrom":[makeQuery(id+"F4.opExtrude","SWEPT_FACE",FACE,{"disambiguationData":[OSD([subQ0])]}),makeQuery(id+"F6.opExtrude","SWEPT_FACE",FACE,{"disambiguationData":[OSD([subQ0])]})]});}
            var sketch = newSketch(context, id + "F9", { "sketchPlane" : qUnion([Q0])});
            skLineSegment(sketch, "E62", {"start": v(-12.69, -75) * mm, "end": v(-40, -75) * mm});
            skLineSegment(sketch, "E63", {"start": v(-12.69, 0) * mm, "end": v(-16.69, 0) * mm});
            skLineSegment(sketch, "E64", {"start": v(-16.69, 0) * mm, "end": v(-40, -75) * mm});
            skLineSegment(sketch, "E65", {"start": v(-40, -115) * mm, "end": v(-36, -115) * mm});
            skLineSegment(sketch, "E66", {"start": v(-36, -115) * mm, "end": v(-36, -111) * mm});
            skCircle(sketch, "E67", {"center": v(-36, -111) * mm, "radius": 3 * mm});
            skLineSegment(sketch, "E68", {"start": v(-36, -115) * mm, "end": v(-32, -115) * mm});
            skLineSegment(sketch, "E69", {"start": v(-32, -115) * mm, "end": v(-12.69, -75) * mm});
            skSolve(sketch);
        }
        {
            var Q0;
            Q0 = qSketchRegion(id + "F9", true);
            var Q1;
            {var subQ0=sQuery(id+"F9.wireOp",EDGE,"E69");Q1=makeQuery(id+"F9.imprint","IMPRINT",FACE,{"disambiguationData":[TD([[makeQuery(id+"F9.imprint","IMPRINT",EDGE,{"derivedFrom":subQ0}),-1.0]])]});}
            var Q2;
            {var subQ0=sQuery(id+"F9.wireOp",EDGE,"E64");Q2=makeQuery(id+"F9.imprint","IMPRINT",FACE,{"disambiguationData":[TD([[makeQuery(id+"F9.imprint","IMPRINT",EDGE,{"derivedFrom":subQ0}),-1.0]])]});}
            extrude(context, id + "F10", {"entities" : qUnion([Q0, Q1, Q2]), "operationType" : NewBodyOperationType.REMOVE, "oppositeDirection" : true, "depth" : 16 * mm, "offsetDistance" : 25 * mm});
        }
        {
            var Q0;
            {var subQ0=sQuery(id+"F3.wireOp",EDGE,"E29");Q0=makeQuery(id+"F6.boolean.opBoolean","MERGE",FACE,{"derivedFrom":[makeQuery(id+"F4.opExtrude","SWEPT_FACE",FACE,{"disambiguationData":[OSD([subQ0])]}),makeQuery(id+"F6.opExtrude","SWEPT_FACE",FACE,{"disambiguationData":[OSD([subQ0])]})]});}
            var sketch = newSketch(context, id + "F11", { "sketchPlane" : qUnion([Q0])});
            skLineSegment(sketch, "E70", {"start": v(12.69, -75) * mm, "end": v(40, -75) * mm});
            skLineSegment(sketch, "E71", {"start": v(40, -115) * mm, "end": v(36, -115) * mm});
            skLineSegment(sketch, "E72", {"start": v(36, -115) * mm, "end": v(36, -111) * mm});
            skLineSegment(sketch, "E73", {"start": v(40, -115) * mm, "end": v(32, -115) * mm});
            skLineSegment(sketch, "E74", {"start": v(32, -115) * mm, "end": v(12.69, -75) * mm});
            skLineSegment(sketch, "E75", {"start": v(12.69, 0) * mm, "end": v(16.69, 0) * mm});
            skLineSegment(sketch, "E76", {"start": v(16.69, 0) * mm, "end": v(40, -75) * mm});
            skCircle(sketch, "E77", {"center": v(36, -111) * mm, "radius": 3 * mm});
            skSolve(sketch);
        }
        {
            var Q0;
            Q0 = qSketchRegion(id + "F11", true);
            var Q1;
            {var subQ0=sQuery(id+"F11.wireOp",EDGE,"E74");Q1=makeQuery(id+"F11.imprint","IMPRINT",FACE,{"disambiguationData":[TD([[makeQuery(id+"F11.imprint","IMPRINT",EDGE,{"derivedFrom":subQ0}),1.0]])]});}
            var Q2;
            {var subQ0=sQuery(id+"F11.wireOp",EDGE,"E76");Q2=makeQuery(id+"F11.imprint","IMPRINT",FACE,{"disambiguationData":[TD([[makeQuery(id+"F11.imprint","IMPRINT",EDGE,{"derivedFrom":subQ0}),1.0]])]});}
            extrude(context, id + "F12", {"entities" : qUnion([Q0, Q1, Q2]), "operationType" : NewBodyOperationType.REMOVE, "oppositeDirection" : true, "depth" : 16 * mm, "offsetDistance" : 25 * mm});
        }
        {
            var Q0;
            {var subQ0=sQuery(id+"F3.wireOp",EDGE,"E43");Q0=makeQuery(id+"F6.boolean.opBoolean","MERGE",FACE,{"derivedFrom":[makeQuery(id+"F4.opExtrude","SWEPT_FACE",FACE,{"disambiguationData":[OSD([subQ0])]}),makeQuery(id+"F6.opExtrude","SWEPT_FACE",FACE,{"disambiguationData":[OSD([subQ0])]})]});}
            var sketch = newSketch(context, id + "F13", { "sketchPlane" : qUnion([Q0])});
            skLineSegment(sketch, "E78.0", {"start": v(-18.1, -24.73) * mm, "end": v(-34, -75.91) * mm});
            skLineSegment(sketch, "E78.1", {"start": v(-34, -105.34) * mm, "end": v(-34, -75.91) * mm});
            skLineSegment(sketch, "E78.2", {"start": v(-34, -105.34) * mm, "end": v(-18.1, -72.4) * mm});
            skLineSegment(sketch, "E79", {"start": v(-18.1, -72.4) * mm, "end": v(-18.1, -24.73) * mm});
            skSolve(sketch);
        }
        {
            var Q0;
            Q0 = qSketchRegion(id + "F13", true);
            extrude(context, id + "F14", {"entities" : qUnion([Q0]), "operationType" : NewBodyOperationType.REMOVE, "oppositeDirection" : true, "depth" : 16 * mm, "offsetDistance" : 25 * mm});
        }
        {
            var Q0;
            {var subQ0=sQuery(id+"F3.wireOp",EDGE,"E40");Q0=makeQuery(id+"F6.boolean.opBoolean","MERGE",FACE,{"derivedFrom":[makeQuery(id+"F4.opExtrude","SWEPT_FACE",FACE,{"disambiguationData":[OSD([subQ0])]}),makeQuery(id+"F6.opExtrude","SWEPT_FACE",FACE,{"disambiguationData":[OSD([subQ0])]})]});}
            var sketch = newSketch(context, id + "F15", { "sketchPlane" : qUnion([Q0])});
            skLineSegment(sketch, "E80.1", {"start": v(-34, -105.34) * mm, "end": v(-34, -75.91) * mm});
            skLineSegment(sketch, "E80.2", {"start": v(-18.69, -26.65) * mm, "end": v(-34, -75.91) * mm});
            skLineSegment(sketch, "E81.0", {"start": v(-18.69, -73.63) * mm, "end": v(-18.69, -26.65) * mm});
            skLineSegment(sketch, "E81.1", {"start": v(-34, -105.34) * mm, "end": v(-18.69, -73.63) * mm});
            skSolve(sketch);
        }
        {
            var Q0;
            Q0 = qSketchRegion(id + "F15", true);
            extrude(context, id + "F16", {"entities" : qUnion([Q0]), "operationType" : NewBodyOperationType.REMOVE, "oppositeDirection" : true, "depth" : 16 * mm, "offsetDistance" : 25 * mm});
        }
        {
            var Q0;
            {var subQ0=sQuery(id+"F3.wireOp",EDGE,"E33");Q0=makeQuery(id+"F6.boolean.opBoolean","MERGE",FACE,{"derivedFrom":[makeQuery(id+"F4.opExtrude","SWEPT_FACE",FACE,{"disambiguationData":[OSD([subQ0])]}),makeQuery(id+"F6.opExtrude","SWEPT_FACE",FACE,{"disambiguationData":[OSD([subQ0])]})]});}
            var sketch = newSketch(context, id + "F17", { "sketchPlane" : qUnion([Q0])});
            skLineSegment(sketch, "E82.0", {"start": v(-18.1, -24.73) * mm, "end": v(-34, -75.91) * mm});
            skLineSegment(sketch, "E82.1", {"start": v(-34, -105.34) * mm, "end": v(-34, -75.91) * mm});
            skLineSegment(sketch, "E82.2", {"start": v(-34, -105.34) * mm, "end": v(-18.1, -72.4) * mm});
            skLineSegment(sketch, "E83", {"start": v(-18.1, -72.4) * mm, "end": v(-18.1, -24.73) * mm});
            skSolve(sketch);
        }
        {
            var Q0;
            Q0 = qSketchRegion(id + "F17", true);
            extrude(context, id + "F18", {"entities" : qUnion([Q0]), "operationType" : NewBodyOperationType.REMOVE, "oppositeDirection" : true, "depth" : 16 * mm, "offsetDistance" : 25 * mm});
        }
        {
            var Q0;
            Q0=makeQuery(id+"F1.opExtrude","CAP_FACE",FACE,{"disambiguationData":[OSD([sQuery(id+"F0.wireOp",EDGE,"E0"),sQuery(id+"F0.wireOp",EDGE,"E4"),sQuery(id+"F0.wireOp",EDGE,"E9"),sQuery(id+"F0.wireOp",EDGE,"E10"),sQuery(id+"F0.wireOp",EDGE,"E11")])],"isStart":false});
            var sketch = newSketch(context, id + "F19", { "sketchPlane" : qUnion([Q0])});
            skCircle(sketch, "E84", {"center": v(0, 0) * mm, "radius": 12.5 * mm});
            skSolve(sketch);
        }
        {
            var Q0;
            Q0 = qSketchRegion(id + "F19", true);
            extrude(context, id + "F20", {"entities" : qUnion([Q0]), "operationType" : NewBodyOperationType.REMOVE, "oppositeDirection" : true, "depth" : 27 * mm, "offsetDistance" : 25 * mm});
        }
        {
            var Q0;
            {var subQ0=sQuery(id+"F3.wireOp",EDGE,"E52");var subQ1=sQuery(id+"F3.wireOp",EDGE,"E51");var subQ2=sQuery(id+"F3.wireOp",EDGE,"E49");var subQ3=sQuery(id+"F3.wireOp",EDGE,"E48");var subQ4=sQuery(id+"F3.wireOp",EDGE,"E47");var subQ5=sQuery(id+"F3.wireOp",EDGE,"E46");var subQ6=sQuery(id+"F3.wireOp",EDGE,"E44");var subQ7=sQuery(id+"F3.wireOp",EDGE,"E43");var subQ8=sQuery(id+"F3.wireOp",EDGE,"E41");var subQ9=sQuery(id+"F3.wireOp",EDGE,"E40");var subQ10=sQuery(id+"F3.wireOp",EDGE,"E37");var subQ11=sQuery(id+"F3.wireOp",EDGE,"E36");var subQ12=sQuery(id+"F3.wireOp",EDGE,"E34");var subQ13=sQuery(id+"F3.wireOp",EDGE,"E33");var subQ14=sQuery(id+"F3.wireOp",EDGE,"E31");var subQ15=sQuery(id+"F3.wireOp",EDGE,"E30");var subQ16=sQuery(id+"F3.wireOp",EDGE,"E29");var subQ17=sQuery(id+"F3.wireOp",EDGE,"E27");var subQ18=makeQuery(id+"F4.opExtrude","CAP_FACE",FACE,{"disambiguationData":[OSD([sQuery(id+"F3.wireOp",EDGE,"E16"),sQuery(id+"F3.wireOp",EDGE,"E17"),sQuery(id+"F3.wireOp",EDGE,"E18"),sQuery(id+"F3.wireOp",EDGE,"E19"),subQ17,sQuery(id+"F3.wireOp",EDGE,"E28"),subQ16,subQ15,subQ14,sQuery(id+"F3.wireOp",EDGE,"E32"),subQ13,subQ12,subQ11,subQ10,sQuery(id+"F3.wireOp",EDGE,"E39"),subQ9,subQ8,sQuery(id+"F3.wireOp",EDGE,"E42"),subQ7,subQ6,sQuery(id+"F3.wireOp",EDGE,"E45"),subQ5,subQ4,subQ3,subQ2,sQuery(id+"F3.wireOp",EDGE,"E50"),subQ1,subQ0])],"isStart":true});var subQ20=sQuery(id+"F0.wireOp",EDGE,"E0");var subQ21=makeQuery(id+"F1.opExtrude","CAP_FACE",FACE,{"disambiguationData":[OSD([subQ20,sQuery(id+"F0.wireOp",EDGE,"E4"),sQuery(id+"F0.wireOp",EDGE,"E9"),sQuery(id+"F0.wireOp",EDGE,"E10"),sQuery(id+"F0.wireOp",EDGE,"E11")])],"isStart":true});var subQ22=makeQuery(id+"F1.opExtrude","SWEPT_FACE",FACE,{"disambiguationData":[OSD([subQ20])]});var subQ23=makeQuery(id+"F4.opExtrude","SWEPT_FACE",FACE,{"disambiguationData":[OSD([subQ5])]});var subQ24=makeQuery(id+"F1.opExtrude","CAP_EDGE",EDGE,{"disambiguationData":[OSD([subQ20])],"isStart":true});var subQ25=makeQuery(id+"F4.opExtrude","SWEPT_FACE",FACE,{"disambiguationData":[OSD([subQ7])]});var subQ26=makeQuery(id+"F4.opExtrude","SWEPT_FACE",FACE,{"disambiguationData":[OSD([subQ1])]});var subQ27=makeQuery(id+"F4.opExtrude","SWEPT_FACE",FACE,{"disambiguationData":[OSD([subQ8,subQ3])]});var subQ28=makeQuery(id+"F4.opExtrude","SWEPT_FACE",FACE,{"disambiguationData":[OSD([subQ13])]});var subQ30=makeQuery(id+"F4.opExtrude","SWEPT_FACE",FACE,{"disambiguationData":[OSD([subQ11,subQ10])]});var subQ31=makeQuery(id+"F4.opExtrude","SWEPT_FACE",FACE,{"disambiguationData":[OSD([subQ9])]});var subQ32=makeQuery(id+"F4.opExtrude","SWEPT_FACE",FACE,{"disambiguationData":[OSD([subQ16])]});var subQ34=makeQuery(id+"F4.opExtrude","SWEPT_FACE",FACE,{"disambiguationData":[OSD([subQ17,subQ15])]});Q0=makeQuery(id+"F12.boolean.opBoolean","MERGE",EDGE,{"derivedFrom":[makeQuery(id+"F4.boolean.opBoolean","SPLIT",EDGE,{"disambiguationData":[topologyDisambiguationEdgeConnected([subQ22,subQ18]),TD([subQ32])],"derivedFrom":subQ24}),makeQuery(id+"F4.boolean.opBoolean","SPLIT",EDGE,{"disambiguationData":[topologyDisambiguationEdgeConnected([subQ22,subQ21]),TD([subQ34])],"derivedFrom":subQ24}),makeQuery(id+"F4.boolean.opBoolean","SPLIT",EDGE,{"disambiguationData":[topologyDisambiguationEdgeConnected([subQ22,subQ18]),TD([subQ28])],"derivedFrom":subQ24}),makeQuery(id+"F10.boolean.opBoolean","MERGE",EDGE,{"derivedFrom":[makeQuery(id+"F4.boolean.opBoolean","SPLIT",EDGE,{"disambiguationData":[topologyDisambiguationEdgeConnected([subQ22,subQ21]),TD([subQ32])],"derivedFrom":subQ24}),makeQuery(id+"F4.boolean.opBoolean","SPLIT",EDGE,{"disambiguationData":[topologyDisambiguationEdgeConnected([subQ22,subQ18]),TD([subQ31])],"derivedFrom":subQ24}),makeQuery(id+"F4.boolean.opBoolean","SPLIT",EDGE,{"disambiguationData":[topologyDisambiguationEdgeConnected([subQ22,subQ21]),TD([subQ30])],"derivedFrom":subQ24}),makeQuery(id+"F4.boolean.opBoolean","SPLIT",EDGE,{"disambiguationData":[topologyDisambiguationEdgeConnected([subQ22,subQ18]),TD([subQ26])],"derivedFrom":subQ24}),makeQuery(id+"F8.boolean.opBoolean","MERGE",EDGE,{"derivedFrom":[makeQuery(id+"F4.boolean.opBoolean","SPLIT",EDGE,{"disambiguationData":[topologyDisambiguationEdgeConnected([subQ22,subQ21]),TD([subQ28])],"derivedFrom":subQ24}),makeQuery(id+"F4.boolean.opBoolean","SPLIT",EDGE,{"disambiguationData":[topologyDisambiguationEdgeConnected([subQ22,subQ18]),TD([subQ25])],"derivedFrom":subQ24}),makeQuery(id+"F4.boolean.opBoolean","SPLIT",EDGE,{"disambiguationData":[topologyDisambiguationEdgeConnected([subQ22,subQ21]),TD([subQ27])],"derivedFrom":subQ24}),makeQuery(id+"F4.boolean.opBoolean","SPLIT",EDGE,{"disambiguationData":[topologyDisambiguationEdgeConnected([subQ22,subQ21]),TD([subQ25])],"derivedFrom":subQ24}),makeQuery(id+"F4.boolean.opBoolean","SPLIT",EDGE,{"disambiguationData":[topologyDisambiguationEdgeConnected([subQ22,subQ18]),TD([subQ23])],"derivedFrom":subQ24})]})]})]});}
            fillet(context, id + "F21", {"entities" : qUnion([Q0]), "radius" : 1 * mm, "tangentPropagation" : true, "allowEdgeOverflow" : false});
        }
        {
            var Q0;
            Q0=qCreatedBy(makeId("Right.planeOp"),FACE);
            var sketch = newSketch(context, id + "F22", { "sketchPlane" : qUnion([Q0])});
            skLineSegment(sketch, "E85", {"start": v(0, 0) * mm, "end": v(0, -5) * mm});
            skCircle(sketch, "E86", {"center": v(0, -5) * mm, "radius": 2.5 * mm});
            skSolve(sketch);
        }
        {
            var Q0;
            Q0 = qSketchRegion(id + "F22", true);
            extrude(context, id + "F23", {"entities" : qUnion([Q0]), "operationType" : NewBodyOperationType.REMOVE, "oppositeDirection" : true, "depth" : 25 * mm, "offsetDistance" : 25 * mm});
        }
    });
